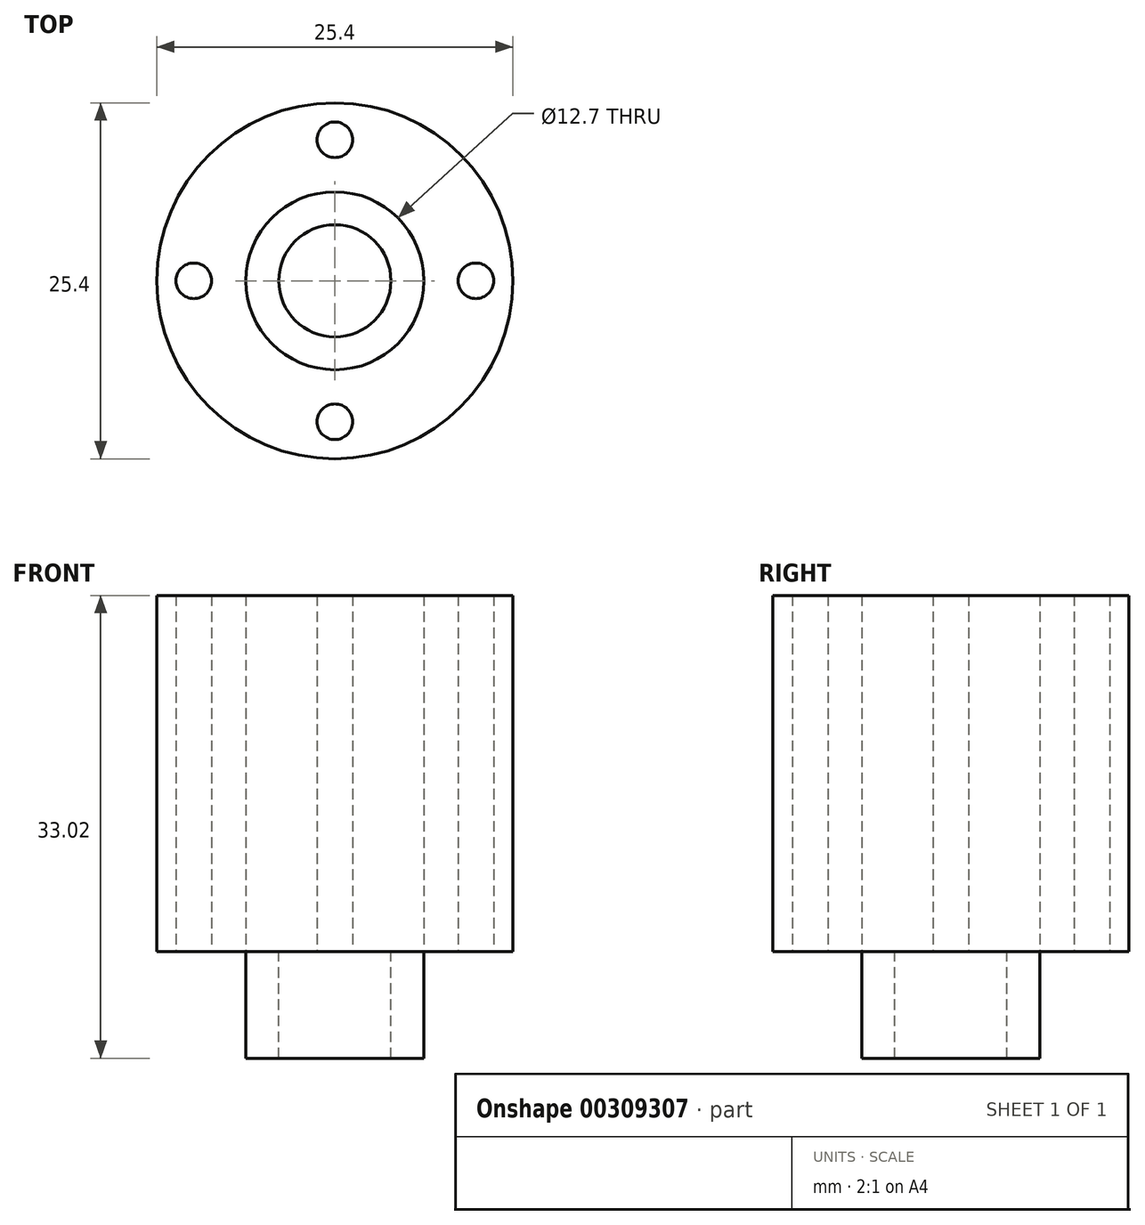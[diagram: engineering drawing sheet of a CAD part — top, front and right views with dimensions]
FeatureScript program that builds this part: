
annotation { "Feature Type Name" : "Feature", "Feature Type Description" : "" }
export const myFeature = defineFeature(function(context is Context, id is Id, definition is map)
    precondition{}
    {
        {
            var Q0;
            Q0=qCreatedBy(makeId("Top.planeOp"),FACE);
            var sketch = newSketch(context, id + "F0", { "sketchPlane" : qUnion([Q0])});
            skCircle(sketch, "E0", {"center": v(0, 0) * mm, "radius": 12.7 * mm});
            skCircle(sketch, "E1", {"center": v(0, 0) * mm, "radius": 6.35 * mm});
            skCircle(sketch, "E2", {"center": v(0, 0) * mm, "radius": 4 * mm});
            skCircle(sketch, "E3", {"center": v(10.06, 0) * mm, "radius": 1.27 * mm});
            skCircle(sketch, "E4", {"center": v(-10.06, 0) * mm, "radius": 1.27 * mm});
            skCircle(sketch, "E5", {"center": v(0, 10.06) * mm, "radius": 1.27 * mm});
            skCircle(sketch, "E6", {"center": v(0, -10.06) * mm, "radius": 1.27 * mm});
            skSolve(sketch);
        }
        {
            var Q0;
            Q0=makeQuery(id+"F0.imprint","IMPRINT",FACE,{"disambiguationData":[TD([[makeQuery(id+"F0.imprint","IMPRINT",EDGE,{"derivedFrom":sQuery(id+"F0.wireOp",EDGE,"E0")}),1.0]])]});
            extrude(context, id + "F1", {"entities" : qUnion([Q0]), "depth" : 25.4 * mm});
        }
        {
            var Q0;
            Q0=makeQuery(id+"F0.imprint","IMPRINT",FACE,{"disambiguationData":[TD([[makeQuery(id+"F0.imprint","IMPRINT",EDGE,{"derivedFrom":sQuery(id+"F0.wireOp",EDGE,"E1")}),1.0]])]});
            extrude(context, id + "F2", {"entities" : qUnion([Q0]), "operationType" : NewBodyOperationType.ADD, "oppositeDirection" : true, "depth" : 7.62 * mm});
        }
    });
